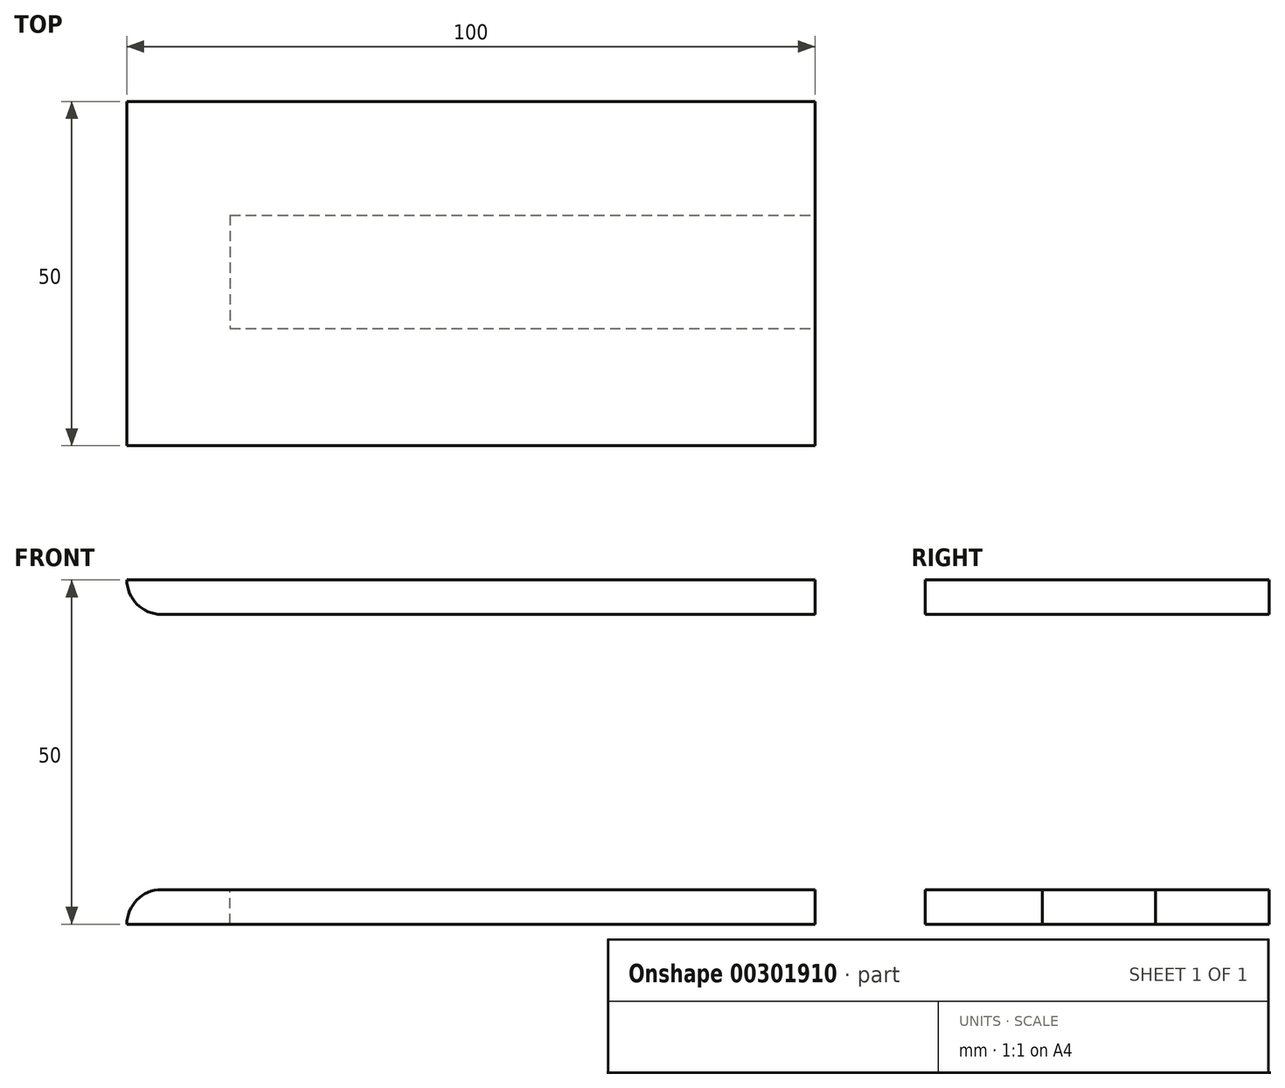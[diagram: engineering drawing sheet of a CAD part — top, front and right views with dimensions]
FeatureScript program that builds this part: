
annotation { "Feature Type Name" : "Feature", "Feature Type Description" : "" }
export const myFeature = defineFeature(function(context is Context, id is Id, definition is map)
    precondition{}
    {
        {
            var Q0;
            Q0=qCreatedBy(makeId("Front.planeOp"),FACE);
            var sketch = newSketch(context, id + "F0", { "sketchPlane" : qUnion([Q0])});
            skLineSegment(sketch, "E0.bottom", {"start": v(0, 0) * mm, "end": v(-100, 0) * mm});
            skLineSegment(sketch, "E0.top", {"start": v(0, 5) * mm, "end": v(-100, 5) * mm});
            skLineSegment(sketch, "E0.left", {"start": v(0, 0) * mm, "end": v(0, 5) * mm});
            skLineSegment(sketch, "E0.right", {"start": v(-100, 0) * mm, "end": v(-100, 5) * mm});
            skLineSegment(sketch, "E1.bottom", {"start": v(0, 5) * mm, "end": v(-10, 5) * mm});
            skLineSegment(sketch, "E1.top", {"start": v(0, 45) * mm, "end": v(-10, 45) * mm});
            skLineSegment(sketch, "E1.left", {"start": v(0, 5) * mm, "end": v(0, 45) * mm});
            skLineSegment(sketch, "E1.right", {"start": v(-10, 5) * mm, "end": v(-10, 45) * mm});
            skLineSegment(sketch, "E2.left", {"start": v(-10, 45) * mm, "end": v(-10, 45) * mm});
            skLineSegment(sketch, "E3.bottom", {"start": v(0, 45) * mm, "end": v(-100, 45) * mm});
            skLineSegment(sketch, "E3.top", {"start": v(0, 50) * mm, "end": v(-100, 50) * mm});
            skLineSegment(sketch, "E3.left", {"start": v(0, 45) * mm, "end": v(0, 50) * mm});
            skLineSegment(sketch, "E3.right", {"start": v(-100, 45) * mm, "end": v(-100, 50) * mm});
            skSolve(sketch);
        }
        {
            var Q0;
            Q0=makeQuery(id+"F0.imprint","IMPRINT",FACE,{"disambiguationData":[TD([[makeQuery(id+"F0.imprint","IMPRINT",EDGE,{"derivedFrom":sQuery(id+"F0.wireOp",EDGE,"E0.bottom")}),-1.0]])]});
            var Q1;
            Q1=makeQuery(id+"F0.imprint","IMPRINT",FACE,{"disambiguationData":[TD([[makeQuery(id+"F0.imprint","IMPRINT",EDGE,{"derivedFrom":sQuery(id+"F0.wireOp",EDGE,"E3.top")}),1.0]])]});
            var Q2;
            Q2=makeQuery(id+"F0.imprint","IMPRINT",FACE,{"disambiguationData":[TD([[makeQuery(id+"F0.imprint","IMPRINT",EDGE,{"derivedFrom":sQuery(id+"F0.wireOp",EDGE,"E1.bottom")}),-1.0]])]});
            extrude(context, id + "F1", {"entities" : qUnion([Q0, Q1, Q2]), "depth" : 50 * mm});
        }
        {
            var Q0;
            Q0=qCreatedBy(makeId("Right.planeOp"),FACE);
            var sketch = newSketch(context, id + "F2", { "sketchPlane" : qUnion([Q0])});
            skLineSegment(sketch, "E4", {"start": v(0, 0) * mm, "end": v(-16.5, 0) * mm});
            skLineSegment(sketch, "E5.bottom", {"start": v(-16.5, 0) * mm, "end": v(-33, 0) * mm});
            skLineSegment(sketch, "E5.top", {"start": v(-16.5, 25) * mm, "end": v(-33, 25) * mm});
            skLineSegment(sketch, "E5.left", {"start": v(-16.5, 0) * mm, "end": v(-16.5, 25) * mm});
            skLineSegment(sketch, "E5.right", {"start": v(-33, 0) * mm, "end": v(-33, 25) * mm});
            skSolve(sketch);
        }
        {
            var Q0;
            Q0=makeQuery(id+"F2.imprint","IMPRINT",FACE,{"disambiguationData":[TD([[makeQuery(id+"F2.imprint","IMPRINT",EDGE,{"derivedFrom":sQuery(id+"F2.wireOp",EDGE,"E5.bottom")}),-1.0]])]});
            extrude(context, id + "F3", {"entities" : qUnion([Q0]), "operationType" : NewBodyOperationType.REMOVE, "oppositeDirection" : true, "depth" : 85 * mm});
        }
        {
            var Q0;
            {var subQ0=sQuery(id+"F0.wireOp",EDGE,"E1.right");var subQ1=sQuery(id+"F0.wireOp",EDGE,"E0.top");Q0=makeQuery(id+"F3.boolean.opBoolean","SPLIT",EDGE,{"disambiguationData":[TD([makeQuery(id+"F3.opExtrude","SWEPT_FACE",FACE,{"disambiguationData":[OSD([sQuery(id+"F2.wireOp",EDGE,"E5.right")])]})])],"derivedFrom":makeQuery(id+"F1.opExtrude","SWEPT_EDGE",EDGE,{"disambiguationData":[OSD([subQ1,sQuery(id+"F0.wireOp",EDGE,"E1.bottom"),subQ0])]})});}
            var Q1;
            {var subQ0=sQuery(id+"F0.wireOp",EDGE,"E1.right");var subQ1=sQuery(id+"F0.wireOp",EDGE,"E0.top");Q1=makeQuery(id+"F3.boolean.opBoolean","SPLIT",EDGE,{"disambiguationData":[TD([makeQuery(id+"F3.opExtrude","SWEPT_FACE",FACE,{"disambiguationData":[OSD([sQuery(id+"F2.wireOp",EDGE,"E5.left")])]})])],"derivedFrom":makeQuery(id+"F1.opExtrude","SWEPT_EDGE",EDGE,{"disambiguationData":[OSD([subQ1,sQuery(id+"F0.wireOp",EDGE,"E1.bottom"),subQ0])]})});}
            var Q2;
            Q2=makeQuery(id+"F1.opExtrude","SWEPT_EDGE",EDGE,{"disambiguationData":[OSD([sQuery(id+"F0.wireOp",EDGE,"E1.right"),sQuery(id+"F0.wireOp",EDGE,"E3.bottom")])]});
            fillet(context, id + "F4", {"entities" : qUnion([Q0, Q1, Q2]), "radius" : 5 * mm, "tangentPropagation" : true, "allowEdgeOverflow" : false});
        }
    });
